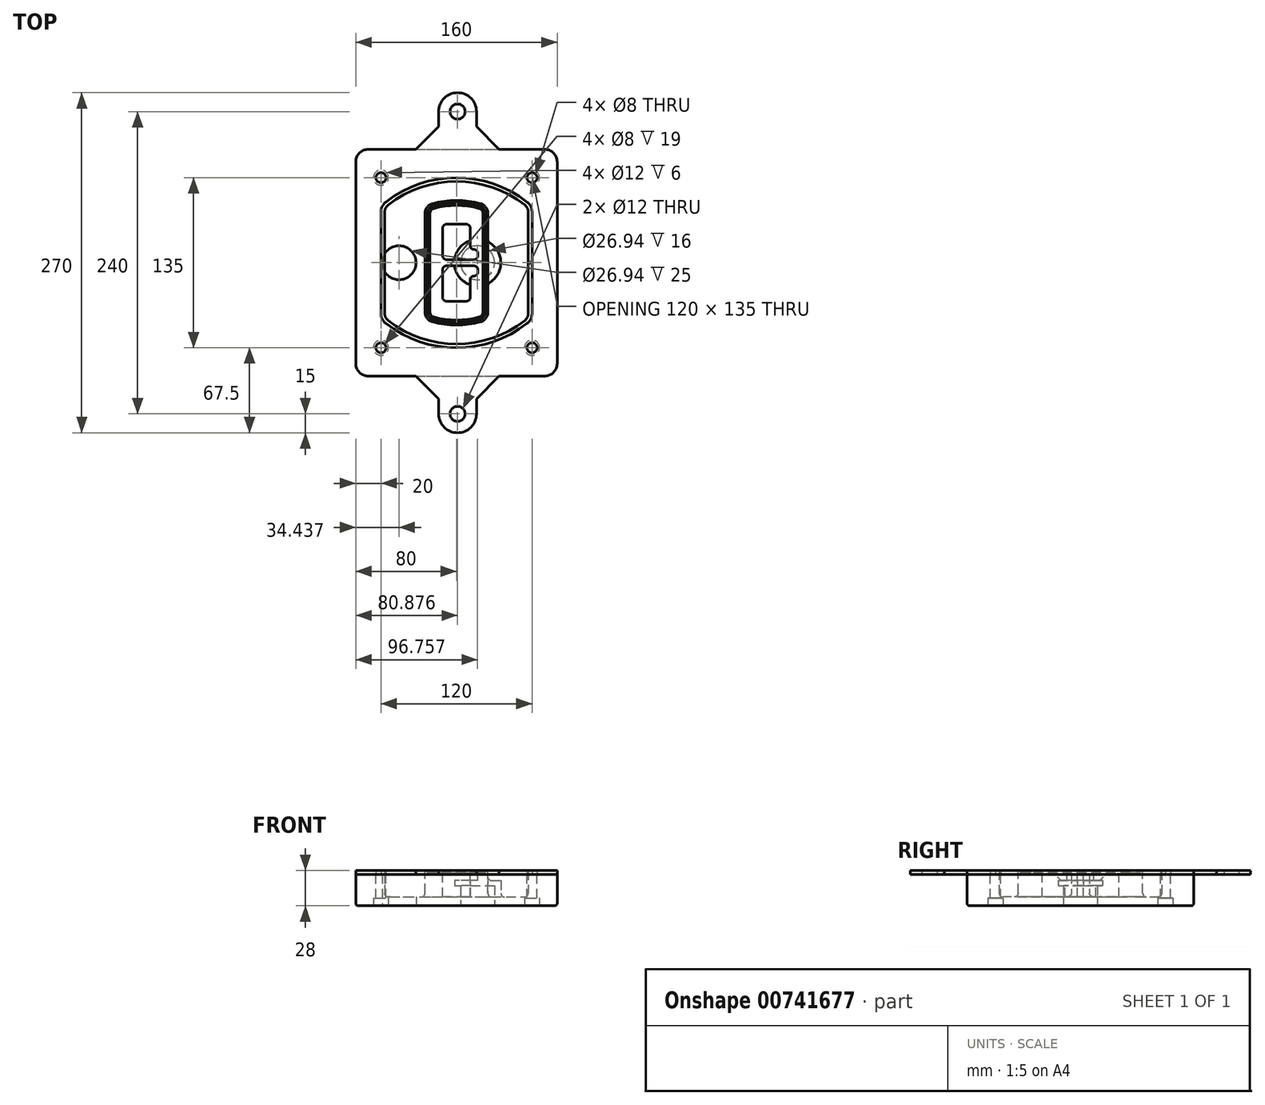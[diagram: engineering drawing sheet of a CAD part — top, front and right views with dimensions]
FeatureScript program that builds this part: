
annotation { "Feature Type Name" : "Feature", "Feature Type Description" : "" }
export const myFeature = defineFeature(function(context is Context, id is Id, definition is map)
    precondition{}
    {
        {
            var Q0;
            Q0=qCreatedBy(makeId("Top.planeOp"),FACE);
            var sketch = newSketch(context, id + "F0", { "sketchPlane" : qUnion([Q0])});
            skPoint(sketch, "E0.rect.middle", {"position": v(0, 0) * mm});
            skLineSegment(sketch, "E1.bottom", {"start": v(-70, -90) * mm, "end": v(70, -90) * mm});
            skLineSegment(sketch, "E1.top", {"start": v(-70, 90) * mm, "end": v(70, 90) * mm});
            skLineSegment(sketch, "E1.left", {"start": v(-80, -80) * mm, "end": v(-80, 80) * mm});
            skLineSegment(sketch, "E1.right", {"start": v(80, -80) * mm, "end": v(80, 80) * mm});
            skLineSegment(sketch, "E2", {"start": v(-80, 90) * mm, "end": v(80, -90) * mm, "construction": true});
            skLineSegment(sketch, "E3", {"start": v(80, 90) * mm, "end": v(-80, -90) * mm, "construction": true});
            skCircle(sketch, "E4", {"center": v(-60, 67.5) * mm, "radius": 4 * mm});
            skCircle(sketch, "E5", {"center": v(60, 67.5) * mm, "radius": 4 * mm});
            skCircle(sketch, "E6", {"center": v(60, -67.5) * mm, "radius": 4 * mm});
            skCircle(sketch, "E7", {"center": v(-60, -67.5) * mm, "radius": 4 * mm});
            skLineSegment(sketch, "E8", {"start": v(-60, 67.5) * mm, "end": v(60, 67.5) * mm, "construction": true});
            skLineSegment(sketch, "E9", {"start": v(60, 67.5) * mm, "end": v(60, -67.5) * mm, "construction": true});
            skLineSegment(sketch, "E10", {"start": v(60, -67.5) * mm, "end": v(-60, -67.5) * mm, "construction": true});
            skLineSegment(sketch, "E11", {"start": v(-60, -67.5) * mm, "end": v(-60, 67.5) * mm, "construction": true});
            skLineSegment(sketch, "E12", {"start": v(-60, 40.3) * mm, "end": v(-60, -40.3) * mm});
            skLineSegment(sketch, "E13", {"start": v(60, 40.3) * mm, "end": v(60, -40.3) * mm});
            skArc(sketch, "E14", {"start": v(56.15, 48.18) * mm, "mid": v(0, 67.5) * mm, "end": v(-56.15, 48.18) * mm});
            skArc(sketch, "E15", {"start": v(-56.15, -48.18) * mm, "mid": v(0, -67.5) * mm, "end": v(56.15, -48.18) * mm});
            skLineSegment(sketch, "E16", {"start": v(-60, 0) * mm, "end": v(60, 0) * mm, "construction": true});
            skPoint(sketch, "E17.visualSharp", {"position": v(-60, -45) * mm});
            skArc(sketch, "E17.filletArc", {"start": v(-60, -40.3) * mm, "mid": v(-58.99, -44.68) * mm, "end": v(-56.15, -48.18) * mm});
            skPoint(sketch, "E18.visualSharp", {"position": v(-60, 45) * mm});
            skArc(sketch, "E18.filletArc", {"start": v(-56.15, 48.18) * mm, "mid": v(-58.99, 44.68) * mm, "end": v(-60, 40.3) * mm});
            skPoint(sketch, "E19.visualSharp", {"position": v(60, 45) * mm});
            skArc(sketch, "E19.filletArc", {"start": v(60, 40.3) * mm, "mid": v(58.99, 44.68) * mm, "end": v(56.15, 48.18) * mm});
            skPoint(sketch, "E20.visualSharp", {"position": v(60, -45) * mm});
            skArc(sketch, "E20.filletArc", {"start": v(56.15, -48.18) * mm, "mid": v(58.99, -44.68) * mm, "end": v(60, -40.3) * mm});
            skPoint(sketch, "E21.visualSharp", {"position": v(-80, 90) * mm});
            skArc(sketch, "E21.filletArc", {"start": v(-70, 90) * mm, "mid": v(-77.07, 87.07) * mm, "end": v(-80, 80) * mm});
            skPoint(sketch, "E22.visualSharp", {"position": v(80, 90) * mm});
            skArc(sketch, "E22.filletArc", {"start": v(80, 80) * mm, "mid": v(77.07, 87.07) * mm, "end": v(70, 90) * mm});
            skPoint(sketch, "E23.visualSharp", {"position": v(80, -90) * mm});
            skArc(sketch, "E23.filletArc", {"start": v(70, -90) * mm, "mid": v(77.07, -87.07) * mm, "end": v(80, -80) * mm});
            skPoint(sketch, "E24.visualSharp", {"position": v(-80, -90) * mm});
            skArc(sketch, "E24.filletArc", {"start": v(-80, -80) * mm, "mid": v(-77.07, -87.07) * mm, "end": v(-70, -90) * mm});
            skArc(sketch, "E25.0", {"start": v(57, 40.3) * mm, "mid": v(56.3, 43.36) * mm, "end": v(54.3, 45.81) * mm});
            skLineSegment(sketch, "E25.1", {"start": v(57, 40.3) * mm, "end": v(57, -40.3) * mm});
            skArc(sketch, "E25.2", {"start": v(54.3, -45.81) * mm, "mid": v(56.3, -43.36) * mm, "end": v(57, -40.3) * mm});
            skArc(sketch, "E25.3", {"start": v(-54.3, -45.81) * mm, "mid": v(0, -64.5) * mm, "end": v(54.3, -45.81) * mm});
            skArc(sketch, "E25.4", {"start": v(-57, -40.3) * mm, "mid": v(-56.3, -43.36) * mm, "end": v(-54.3, -45.81) * mm});
            skArc(sketch, "E25.5", {"start": v(54.3, 45.81) * mm, "mid": v(0, 64.5) * mm, "end": v(-54.3, 45.81) * mm});
            skLineSegment(sketch, "E25.6", {"start": v(-57, 40.3) * mm, "end": v(-57, -40.3) * mm});
            skArc(sketch, "E25.7", {"start": v(-54.3, 45.81) * mm, "mid": v(-56.3, 43.36) * mm, "end": v(-57, 40.3) * mm});
            skArc(sketch, "E26.0", {"start": v(-58.62, 51.33) * mm, "mid": v(-62.58, 46.43) * mm, "end": v(-64, 40.3) * mm});
            skArc(sketch, "E26.1", {"start": v(58.62, 51.33) * mm, "mid": v(0, 71.5) * mm, "end": v(-58.62, 51.33) * mm});
            skArc(sketch, "E26.2", {"start": v(64, 40.3) * mm, "mid": v(62.58, 46.43) * mm, "end": v(58.62, 51.33) * mm});
            skLineSegment(sketch, "E26.3", {"start": v(64, 40.3) * mm, "end": v(64, -40.3) * mm});
            skArc(sketch, "E26.4", {"start": v(58.62, -51.33) * mm, "mid": v(62.58, -46.43) * mm, "end": v(64, -40.3) * mm});
            skLineSegment(sketch, "E26.5", {"start": v(-64, 40.3) * mm, "end": v(-64, -40.3) * mm});
            skArc(sketch, "E26.6", {"start": v(-58.62, -51.33) * mm, "mid": v(0, -71.5) * mm, "end": v(58.62, -51.33) * mm});
            skArc(sketch, "E26.7", {"start": v(-64, -40.3) * mm, "mid": v(-62.58, -46.43) * mm, "end": v(-58.62, -51.33) * mm});
            skSolve(sketch);
        }
        {
            var Q0;
            Q0=makeQuery(id+"F0.imprint","IMPRINT",FACE,{"disambiguationData":[TD([[makeQuery(id+"F0.imprint","IMPRINT",EDGE,{"derivedFrom":sQuery(id+"F0.wireOp",EDGE,"E1.bottom")}),1.0]])]});
            var Q1;
            Q1=makeQuery(id+"F0.imprint","IMPRINT",FACE,{"disambiguationData":[TD([[makeQuery(id+"F0.imprint","IMPRINT",EDGE,{"derivedFrom":sQuery(id+"F0.wireOp",EDGE,"E12")}),1.0]])]});
            var Q2;
            Q2=makeQuery(id+"F0.imprint","IMPRINT",FACE,{"disambiguationData":[TD([[makeQuery(id+"F0.imprint","IMPRINT",EDGE,{"derivedFrom":sQuery(id+"F0.wireOp",EDGE,"E25.0")}),1.0]])]});
            var Q3;
            Q3=makeQuery(id+"F0.imprint","IMPRINT",FACE,{"disambiguationData":[TD([[makeQuery(id+"F0.imprint","IMPRINT",EDGE,{"derivedFrom":sQuery(id+"F0.wireOp",EDGE,"E12")}),-1.0]])]});
            extrude(context, id + "F1", {"entities" : qUnion([Q0, Q1, Q2, Q3]), "oppositeDirection" : true, "depth" : 25 * mm});
        }
        {
            var Q0;
            Q0=makeQuery(id+"F0.imprint","IMPRINT",FACE,{"disambiguationData":[TD([[makeQuery(id+"F0.imprint","IMPRINT",EDGE,{"derivedFrom":sQuery(id+"F0.wireOp",EDGE,"E12")}),1.0]])]});
            extrude(context, id + "F2", {"entities" : qUnion([Q0]), "operationType" : NewBodyOperationType.ADD, "depth" : 3 * mm});
        }
        {
            var Q0;
            Q0=makeQuery(id+"F0.imprint","IMPRINT",FACE,{"disambiguationData":[TD([[makeQuery(id+"F0.imprint","IMPRINT",EDGE,{"derivedFrom":sQuery(id+"F0.wireOp",EDGE,"E25.0")}),1.0]])]});
            extrude(context, id + "F3", {"entities" : qUnion([Q0]), "operationType" : NewBodyOperationType.REMOVE, "oppositeDirection" : true, "depth" : 18 * mm});
        }
        {
            var Q0;
            Q0=makeQuery(id+"F2.opExtrude","CAP_FACE",FACE,{"disambiguationData":[OSD([sQuery(id+"F0.wireOp",EDGE,"E12"),sQuery(id+"F0.wireOp",EDGE,"E13"),sQuery(id+"F0.wireOp",EDGE,"E14"),sQuery(id+"F0.wireOp",EDGE,"E15"),sQuery(id+"F0.wireOp",EDGE,"E17.filletArc"),sQuery(id+"F0.wireOp",EDGE,"E18.filletArc"),sQuery(id+"F0.wireOp",EDGE,"E19.filletArc"),sQuery(id+"F0.wireOp",EDGE,"E20.filletArc"),sQuery(id+"F0.wireOp",EDGE,"E25.0"),sQuery(id+"F0.wireOp",EDGE,"E25.1"),sQuery(id+"F0.wireOp",EDGE,"E25.2"),sQuery(id+"F0.wireOp",EDGE,"E25.3"),sQuery(id+"F0.wireOp",EDGE,"E25.4"),sQuery(id+"F0.wireOp",EDGE,"E25.5"),sQuery(id+"F0.wireOp",EDGE,"E25.6"),sQuery(id+"F0.wireOp",EDGE,"E25.7")])],"isStart":false});
            var sketch = newSketch(context, id + "F4", { "sketchPlane" : qUnion([Q0])});
            skArc(sketch, "E27.0", {"start": v(-19.08, -46.97) * mm, "mid": v(0, -49.5) * mm, "end": v(19.08, -46.97) * mm});
            skArc(sketch, "E28.0", {"start": v(19.08, 46.97) * mm, "mid": v(0, 49.5) * mm, "end": v(-19.08, 46.97) * mm});
            skLineSegment(sketch, "E29", {"start": v(-25, 39.25) * mm, "end": v(-25, -39.25) * mm});
            skLineSegment(sketch, "E30", {"start": v(25, 39.25) * mm, "end": v(25, -39.25) * mm});
            skLineSegment(sketch, "E31", {"start": v(-25, 45.1) * mm, "end": v(25, 45.1) * mm, "construction": true});
            skLineSegment(sketch, "E32", {"start": v(-25, -45.1) * mm, "end": v(25, -45.1) * mm, "construction": true});
            skPoint(sketch, "E33.visualSharp", {"position": v(-25, 45.1) * mm});
            skArc(sketch, "E33.filletArc", {"start": v(-19.08, 46.97) * mm, "mid": v(-23.35, 44.11) * mm, "end": v(-25, 39.25) * mm});
            skPoint(sketch, "E34.visualSharp", {"position": v(25, 45.1) * mm});
            skArc(sketch, "E34.filletArc", {"start": v(25, 39.25) * mm, "mid": v(23.35, 44.11) * mm, "end": v(19.08, 46.97) * mm});
            skPoint(sketch, "E35.visualSharp", {"position": v(25, -45.1) * mm});
            skArc(sketch, "E35.filletArc", {"start": v(19.08, -46.97) * mm, "mid": v(23.35, -44.11) * mm, "end": v(25, -39.25) * mm});
            skPoint(sketch, "E36.visualSharp", {"position": v(-25, -45.1) * mm});
            skArc(sketch, "E36.filletArc", {"start": v(-25, -39.25) * mm, "mid": v(-23.35, -44.11) * mm, "end": v(-19.08, -46.97) * mm});
            skArc(sketch, "E37.0", {"start": v(54.3, 45.81) * mm, "mid": v(0, 64.5) * mm, "end": v(-54.3, 45.81) * mm});
            skArc(sketch, "E37.1", {"start": v(-54.3, 45.81) * mm, "mid": v(-56.3, 43.36) * mm, "end": v(-57, 40.3) * mm});
            skLineSegment(sketch, "E37.2", {"start": v(-57, 40.3) * mm, "end": v(-57, -40.3) * mm});
            skArc(sketch, "E37.3", {"start": v(-57, -40.3) * mm, "mid": v(-56.3, -43.36) * mm, "end": v(-54.3, -45.81) * mm});
            skArc(sketch, "E37.4", {"start": v(-54.3, -45.81) * mm, "mid": v(0, -64.5) * mm, "end": v(54.3, -45.81) * mm});
            skArc(sketch, "E37.5", {"start": v(54.3, -45.81) * mm, "mid": v(56.3, -43.36) * mm, "end": v(57, -40.3) * mm});
            skLineSegment(sketch, "E37.6", {"start": v(57, 40.3) * mm, "end": v(57, -40.3) * mm});
            skArc(sketch, "E37.7", {"start": v(57, 40.3) * mm, "mid": v(56.3, 43.36) * mm, "end": v(54.3, 45.81) * mm});
            skLineSegment(sketch, "E38.0", {"start": v(23, 39.25) * mm, "end": v(23, -39.25) * mm});
            skArc(sketch, "E38.1", {"start": v(18.56, -45.04) * mm, "mid": v(21.76, -42.9) * mm, "end": v(23, -39.25) * mm});
            skArc(sketch, "E38.2", {"start": v(-18.56, -45.04) * mm, "mid": v(0, -47.5) * mm, "end": v(18.56, -45.04) * mm});
            skArc(sketch, "E38.3", {"start": v(-23, -39.25) * mm, "mid": v(-21.76, -42.9) * mm, "end": v(-18.56, -45.04) * mm});
            skLineSegment(sketch, "E38.4", {"start": v(-23, 39.25) * mm, "end": v(-23, -39.25) * mm});
            skArc(sketch, "E38.5", {"start": v(23, 39.25) * mm, "mid": v(21.76, 42.9) * mm, "end": v(18.56, 45.04) * mm});
            skArc(sketch, "E38.6", {"start": v(-18.56, 45.04) * mm, "mid": v(-21.76, 42.9) * mm, "end": v(-23, 39.25) * mm});
            skArc(sketch, "E38.7", {"start": v(18.56, 45.04) * mm, "mid": v(0, 47.5) * mm, "end": v(-18.56, 45.04) * mm});
            skArc(sketch, "E39.0", {"start": v(21, 39.25) * mm, "mid": v(20.18, 41.68) * mm, "end": v(18.04, 43.1) * mm});
            skLineSegment(sketch, "E39.1", {"start": v(21, 39.25) * mm, "end": v(21, -39.25) * mm});
            skArc(sketch, "E39.2", {"start": v(18.04, -43.1) * mm, "mid": v(20.18, -41.68) * mm, "end": v(21, -39.25) * mm});
            skArc(sketch, "E39.3", {"start": v(-18.04, -43.1) * mm, "mid": v(0, -45.5) * mm, "end": v(18.04, -43.1) * mm});
            skArc(sketch, "E39.4", {"start": v(-21, -39.25) * mm, "mid": v(-20.18, -41.68) * mm, "end": v(-18.04, -43.1) * mm});
            skArc(sketch, "E39.5", {"start": v(18.04, 43.1) * mm, "mid": v(0, 45.5) * mm, "end": v(-18.04, 43.1) * mm});
            skLineSegment(sketch, "E39.6", {"start": v(-21, 39.25) * mm, "end": v(-21, -39.25) * mm});
            skArc(sketch, "E39.7", {"start": v(-18.04, 43.1) * mm, "mid": v(-20.18, 41.68) * mm, "end": v(-21, 39.25) * mm});
            skLineSegment(sketch, "E40", {"start": v(-25, 0) * mm, "end": v(25, 0) * mm, "construction": true});
            skLineSegment(sketch, "E41", {"start": v(-11, 5.5) * mm, "end": v(-11, 27.5) * mm});
            skLineSegment(sketch, "E42", {"start": v(-8, 30.5) * mm, "end": v(8, 30.5) * mm});
            skLineSegment(sketch, "E43", {"start": v(11, 27.5) * mm, "end": v(11, 13.5) * mm});
            skLineSegment(sketch, "E44", {"start": v(14, 10.5) * mm, "end": v(14, 10.5) * mm});
            skLineSegment(sketch, "E45", {"start": v(17, 7.5) * mm, "end": v(17, 5.5) * mm});
            skLineSegment(sketch, "E46", {"start": v(14, 2.5) * mm, "end": v(-8, 2.5) * mm});
            skPoint(sketch, "E47.visualSharp", {"position": v(-11, 30.5) * mm});
            skArc(sketch, "E47.filletArc", {"start": v(-8, 30.5) * mm, "mid": v(-10.12, 29.62) * mm, "end": v(-11, 27.5) * mm});
            skPoint(sketch, "E48.visualSharp", {"position": v(11, 30.5) * mm});
            skArc(sketch, "E48.filletArc", {"start": v(11, 27.5) * mm, "mid": v(10.12, 29.62) * mm, "end": v(8, 30.5) * mm});
            skPoint(sketch, "E49.visualSharp", {"position": v(11, 10.5) * mm});
            skArc(sketch, "E49.filletArc", {"start": v(11, 13.5) * mm, "mid": v(11.88, 11.38) * mm, "end": v(14, 10.5) * mm});
            skPoint(sketch, "E50.visualSharp", {"position": v(17, 10.5) * mm});
            skArc(sketch, "E50.filletArc", {"start": v(17, 7.5) * mm, "mid": v(16.12, 9.62) * mm, "end": v(14, 10.5) * mm});
            skPoint(sketch, "E51.visualSharp", {"position": v(17, 2.5) * mm});
            skArc(sketch, "E51.filletArc", {"start": v(14, 2.5) * mm, "mid": v(16.12, 3.38) * mm, "end": v(17, 5.5) * mm});
            skPoint(sketch, "E52.visualSharp", {"position": v(-11, 2.5) * mm});
            skArc(sketch, "E52.filletArc", {"start": v(-11, 5.5) * mm, "mid": v(-10.12, 3.38) * mm, "end": v(-8, 2.5) * mm});
            skLineSegment(sketch, "E53.0.MirrorCS", {"start": v(14, -2.5) * mm, "end": v(-8, -2.5) * mm});
            skArc(sketch, "E54.0.MirrorCS", {"start": v(-11, -5.5) * mm, "mid": v(-10.12, -3.38) * mm, "end": v(-8, -2.5) * mm});
            skLineSegment(sketch, "E55.0.MirrorCS", {"start": v(-11, -5.5) * mm, "end": v(-11, -27.5) * mm});
            skArc(sketch, "E56.0.MirrorCS", {"start": v(-8, -30.5) * mm, "mid": v(-10.12, -29.62) * mm, "end": v(-11, -27.5) * mm});
            skLineSegment(sketch, "E57.0.MirrorCS", {"start": v(-8, -30.5) * mm, "end": v(8, -30.5) * mm});
            skArc(sketch, "E58.0.MirrorCS", {"start": v(11, -27.5) * mm, "mid": v(10.12, -29.62) * mm, "end": v(8, -30.5) * mm});
            skLineSegment(sketch, "E59.0.MirrorCS", {"start": v(11, -27.5) * mm, "end": v(11, -13.5) * mm});
            skArc(sketch, "E60.0.MirrorCS", {"start": v(11, -13.5) * mm, "mid": v(11.88, -11.38) * mm, "end": v(14, -10.5) * mm});
            skArc(sketch, "E61.0.MirrorCS", {"start": v(17, -7.5) * mm, "mid": v(16.12, -9.62) * mm, "end": v(14, -10.5) * mm});
            skLineSegment(sketch, "E62.0.MirrorCS", {"start": v(17, -7.5) * mm, "end": v(17, -5.5) * mm});
            skArc(sketch, "E63.0.MirrorCS", {"start": v(14, -2.5) * mm, "mid": v(16.12, -3.38) * mm, "end": v(17, -5.5) * mm});
            skSolve(sketch);
        }
        {
            var Q0;
            Q0=makeQuery(id+"F4.imprint","IMPRINT",FACE,{"disambiguationData":[TD([[makeQuery(id+"F4.imprint","IMPRINT",EDGE,{"derivedFrom":sQuery(id+"F4.wireOp",EDGE,"E27.0")}),1.0]])]});
            var Q1;
            Q1=makeQuery(id+"F4.imprint","IMPRINT",FACE,{"disambiguationData":[TD([[makeQuery(id+"F4.imprint","IMPRINT",EDGE,{"derivedFrom":sQuery(id+"F4.wireOp",EDGE,"E38.0")}),-1.0]])]});
            var Q2;
            Q2=makeQuery(id+"F4.imprint","IMPRINT",FACE,{"disambiguationData":[TD([[makeQuery(id+"F4.imprint","IMPRINT",EDGE,{"derivedFrom":sQuery(id+"F4.wireOp",EDGE,"E39.0")}),1.0]])]});
            extrude(context, id + "F5", {"entities" : qUnion([Q0, Q1, Q2]), "operationType" : NewBodyOperationType.ADD, "endBound" : BoundingType.UP_TO_NEXT, "oppositeDirection" : true, "depth" : 25 * mm});
        }
        {
            var Q0;
            Q0=makeQuery(id+"F4.imprint","IMPRINT",FACE,{"disambiguationData":[TD([[makeQuery(id+"F4.imprint","IMPRINT",EDGE,{"derivedFrom":sQuery(id+"F4.wireOp",EDGE,"E38.0")}),-1.0]])]});
            extrude(context, id + "F6", {"entities" : qUnion([Q0]), "operationType" : NewBodyOperationType.REMOVE, "oppositeDirection" : true, "depth" : 2 * mm});
        }
        {
            var Q0;
            Q0=makeQuery(id+"F1.opExtrude","CAP_FACE",FACE,{"disambiguationData":[OSD([sQuery(id+"F0.wireOp",EDGE,"E1.bottom"),sQuery(id+"F0.wireOp",EDGE,"E1.top"),sQuery(id+"F0.wireOp",EDGE,"E1.left"),sQuery(id+"F0.wireOp",EDGE,"E1.right"),sQuery(id+"F0.wireOp",EDGE,"E4"),sQuery(id+"F0.wireOp",EDGE,"E5"),sQuery(id+"F0.wireOp",EDGE,"E6"),sQuery(id+"F0.wireOp",EDGE,"E7"),sQuery(id+"F0.wireOp",EDGE,"E21.filletArc"),sQuery(id+"F0.wireOp",EDGE,"E22.filletArc"),sQuery(id+"F0.wireOp",EDGE,"E23.filletArc"),sQuery(id+"F0.wireOp",EDGE,"E24.filletArc")])],"isStart":false});
            var sketch = newSketch(context, id + "F7", { "sketchPlane" : qUnion([Q0])});
            skCircle(sketch, "E64", {"center": v(16.76, 0) * mm, "radius": 13.47 * mm});
            skCircle(sketch, "E65", {"center": v(-45.56, 0) * mm, "radius": 13.47 * mm});
            skLineSegment(sketch, "E66", {"start": v(80, 0) * mm, "end": v(-80, 0) * mm});
            skCircle(sketch, "E67", {"center": v(16.76, 0) * mm, "radius": 18.47 * mm});
            skCircle(sketch, "E68", {"center": v(60, -67.5) * mm, "radius": 6 * mm});
            skCircle(sketch, "E69", {"center": v(-60, -67.5) * mm, "radius": 6 * mm});
            skCircle(sketch, "E70", {"center": v(-60, 67.5) * mm, "radius": 6 * mm});
            skCircle(sketch, "E71", {"center": v(60, 67.5) * mm, "radius": 6 * mm});
            skSolve(sketch);
        }
        {
            var Q0;
            {var subQ1=sQuery(id+"F7.wireOp",EDGE,"E66");var subQ4=sQuery(id+"F7.wireOp",EDGE,"E64");var subQ6=makeQuery(id+"F7.imprint","INTERSECT",VERTEX,{"disambiguationData":[OD(0.0)],"derivedFrom":[subQ4,subQ1]});Q0=makeQuery(id+"F7.imprint","IMPRINT",FACE,{"disambiguationData":[TD([[makeQuery(id+"F7.imprint","IMPRINT",EDGE,{"disambiguationData":[TD([[subQ6,-1.0]])],"derivedFrom":subQ4}),-1.0]])]});}
            var Q1;
            {var subQ0=sQuery(id+"F7.wireOp",EDGE,"E66");var subQ1=sQuery(id+"F7.wireOp",EDGE,"E64");var subQ3=makeQuery(id+"F7.imprint","INTERSECT",VERTEX,{"disambiguationData":[OD(0.0)],"derivedFrom":[subQ1,subQ0]});Q1=makeQuery(id+"F7.imprint","IMPRINT",FACE,{"disambiguationData":[TD([[makeQuery(id+"F7.imprint","IMPRINT",EDGE,{"disambiguationData":[TD([[subQ3,-1.0]])],"derivedFrom":subQ1}),1.0]])]});}
            var Q2;
            {var subQ0=sQuery(id+"F7.wireOp",EDGE,"E66");var subQ1=sQuery(id+"F7.wireOp",EDGE,"E64");var subQ3=makeQuery(id+"F7.imprint","INTERSECT",VERTEX,{"disambiguationData":[OD(0.0)],"derivedFrom":[subQ1,subQ0]});Q2=makeQuery(id+"F7.imprint","IMPRINT",FACE,{"disambiguationData":[TD([[makeQuery(id+"F7.imprint","IMPRINT",EDGE,{"disambiguationData":[TD([[subQ3,1.0]])],"derivedFrom":subQ1}),1.0]])]});}
            var Q3;
            {var subQ1=sQuery(id+"F7.wireOp",EDGE,"E66");var subQ4=sQuery(id+"F7.wireOp",EDGE,"E64");var subQ6=makeQuery(id+"F7.imprint","INTERSECT",VERTEX,{"disambiguationData":[OD(0.0)],"derivedFrom":[subQ4,subQ1]});Q3=makeQuery(id+"F7.imprint","IMPRINT",FACE,{"disambiguationData":[TD([[makeQuery(id+"F7.imprint","IMPRINT",EDGE,{"disambiguationData":[TD([[subQ6,1.0]])],"derivedFrom":subQ4}),-1.0]])]});}
            extrude(context, id + "F8", {"entities" : qUnion([Q0, Q1, Q2, Q3]), "operationType" : NewBodyOperationType.ADD, "oppositeDirection" : true, "depth" : 20 * mm});
        }
        {
            var Q0;
            {var subQ0=sQuery(id+"F7.wireOp",EDGE,"E66");var subQ1=sQuery(id+"F7.wireOp",EDGE,"E64");var subQ3=makeQuery(id+"F7.imprint","INTERSECT",VERTEX,{"disambiguationData":[OD(0.0)],"derivedFrom":[subQ1,subQ0]});Q0=makeQuery(id+"F7.imprint","IMPRINT",FACE,{"disambiguationData":[TD([[makeQuery(id+"F7.imprint","IMPRINT",EDGE,{"disambiguationData":[TD([[subQ3,-1.0]])],"derivedFrom":subQ1}),1.0]])]});}
            var Q1;
            {var subQ0=sQuery(id+"F7.wireOp",EDGE,"E66");var subQ1=sQuery(id+"F7.wireOp",EDGE,"E64");var subQ3=makeQuery(id+"F7.imprint","INTERSECT",VERTEX,{"disambiguationData":[OD(0.0)],"derivedFrom":[subQ1,subQ0]});Q1=makeQuery(id+"F7.imprint","IMPRINT",FACE,{"disambiguationData":[TD([[makeQuery(id+"F7.imprint","IMPRINT",EDGE,{"disambiguationData":[TD([[subQ3,1.0]])],"derivedFrom":subQ1}),1.0]])]});}
            extrude(context, id + "F9", {"entities" : qUnion([Q0, Q1]), "operationType" : NewBodyOperationType.REMOVE, "oppositeDirection" : true, "depth" : 16 * mm});
        }
        {
            var Q0;
            {var subQ0=sQuery(id+"F7.wireOp",EDGE,"E66");var subQ1=sQuery(id+"F7.wireOp",EDGE,"E65");var subQ3=makeQuery(id+"F7.imprint","INTERSECT",VERTEX,{"disambiguationData":[OD(0.0)],"derivedFrom":[subQ1,subQ0]});Q0=makeQuery(id+"F7.imprint","IMPRINT",FACE,{"disambiguationData":[TD([[makeQuery(id+"F7.imprint","IMPRINT",EDGE,{"disambiguationData":[TD([[subQ3,-1.0]])],"derivedFrom":subQ1}),1.0]])]});}
            var Q1;
            {var subQ0=sQuery(id+"F7.wireOp",EDGE,"E66");var subQ1=sQuery(id+"F7.wireOp",EDGE,"E65");var subQ3=makeQuery(id+"F7.imprint","INTERSECT",VERTEX,{"disambiguationData":[OD(0.0)],"derivedFrom":[subQ1,subQ0]});Q1=makeQuery(id+"F7.imprint","IMPRINT",FACE,{"disambiguationData":[TD([[makeQuery(id+"F7.imprint","IMPRINT",EDGE,{"disambiguationData":[TD([[subQ3,1.0]])],"derivedFrom":subQ1}),1.0]])]});}
            extrude(context, id + "F10", {"entities" : qUnion([Q0, Q1]), "operationType" : NewBodyOperationType.REMOVE, "oppositeDirection" : true, "depth" : 25 * mm});
        }
        {
            var Q0;
            Q0=makeQuery(id+"F7.imprint","IMPRINT",FACE,{"disambiguationData":[TD([[makeQuery(id+"F7.imprint","IMPRINT",EDGE,{"derivedFrom":sQuery(id+"F7.wireOp",EDGE,"E68")}),1.0]])]});
            var Q1;
            Q1=makeQuery(id+"F7.imprint","IMPRINT",FACE,{"disambiguationData":[TD([[makeQuery(id+"F7.imprint","IMPRINT",EDGE,{"derivedFrom":makeQuery(id+"F1.opExtrude","CAP_EDGE",EDGE,{"disambiguationData":[OSD([sQuery(id+"F0.wireOp",EDGE,"E5")])],"isStart":false})}),-1.0]])]});
            var Q2;
            Q2=makeQuery(id+"F7.imprint","IMPRINT",FACE,{"disambiguationData":[TD([[makeQuery(id+"F7.imprint","IMPRINT",EDGE,{"derivedFrom":sQuery(id+"F7.wireOp",EDGE,"E69")}),1.0]])]});
            var Q3;
            Q3=makeQuery(id+"F7.imprint","IMPRINT",FACE,{"disambiguationData":[TD([[makeQuery(id+"F7.imprint","IMPRINT",EDGE,{"derivedFrom":makeQuery(id+"F1.opExtrude","CAP_EDGE",EDGE,{"disambiguationData":[OSD([sQuery(id+"F0.wireOp",EDGE,"E4")])],"isStart":false})}),-1.0]])]});
            var Q4;
            Q4=makeQuery(id+"F7.imprint","IMPRINT",FACE,{"disambiguationData":[TD([[makeQuery(id+"F7.imprint","IMPRINT",EDGE,{"derivedFrom":sQuery(id+"F7.wireOp",EDGE,"E70")}),1.0]])]});
            var Q5;
            Q5=makeQuery(id+"F7.imprint","IMPRINT",FACE,{"disambiguationData":[TD([[makeQuery(id+"F7.imprint","IMPRINT",EDGE,{"derivedFrom":makeQuery(id+"F1.opExtrude","CAP_EDGE",EDGE,{"disambiguationData":[OSD([sQuery(id+"F0.wireOp",EDGE,"E7")])],"isStart":false})}),-1.0]])]});
            var Q6;
            Q6=makeQuery(id+"F7.imprint","IMPRINT",FACE,{"disambiguationData":[TD([[makeQuery(id+"F7.imprint","IMPRINT",EDGE,{"derivedFrom":sQuery(id+"F7.wireOp",EDGE,"E71")}),1.0]])]});
            var Q7;
            Q7=makeQuery(id+"F7.imprint","IMPRINT",FACE,{"disambiguationData":[TD([[makeQuery(id+"F7.imprint","IMPRINT",EDGE,{"derivedFrom":makeQuery(id+"F1.opExtrude","CAP_EDGE",EDGE,{"disambiguationData":[OSD([sQuery(id+"F0.wireOp",EDGE,"E6")])],"isStart":false})}),-1.0]])]});
            extrude(context, id + "F11", {"entities" : qUnion([Q0, Q1, Q2, Q3, Q4, Q5, Q6, Q7]), "operationType" : NewBodyOperationType.REMOVE, "oppositeDirection" : true, "depth" : 6 * mm});
        }
        {
            var Q0;
            Q0=makeQuery(id+"F9.boolean.opBoolean","COPY",FACE,{"derivedFrom":makeQuery(id+"F9.opExtrude","CAP_FACE",FACE,{"disambiguationData":[OSD([sQuery(id+"F7.wireOp",EDGE,"E64")])],"isStart":false})});
            var sketch = newSketch(context, id + "F12", { "sketchPlane" : qUnion([Q0])});
            skArc(sketch, "E72.0", {"start": v(11, 17.55) * mm, "mid": v(2.57, 11.82) * mm, "end": v(-1.54, 2.5) * mm});
            skArc(sketch, "E72.1", {"start": v(-1.54, -2.5) * mm, "mid": v(2.57, -11.82) * mm, "end": v(11, -17.55) * mm});
            skLineSegment(sketch, "E73", {"start": v(-1.54, -2.5) * mm, "end": v(14, -2.5) * mm});
            skLineSegment(sketch, "E74.0", {"start": v(14, 2.5) * mm, "end": v(-1.54, 2.5) * mm});
            skArc(sketch, "E74.1", {"start": v(14, 2.5) * mm, "mid": v(16.12, 3.38) * mm, "end": v(17, 5.5) * mm});
            skLineSegment(sketch, "E74.2", {"start": v(17, 7.5) * mm, "end": v(17, 5.5) * mm});
            skArc(sketch, "E74.3", {"start": v(17, 7.5) * mm, "mid": v(16.12, 9.62) * mm, "end": v(14, 10.5) * mm});
            skArc(sketch, "E74.4", {"start": v(11, 13.5) * mm, "mid": v(11.88, 11.38) * mm, "end": v(14, 10.5) * mm});
            skLineSegment(sketch, "E74.5", {"start": v(11, 17.55) * mm, "end": v(11, 13.5) * mm});
            skLineSegment(sketch, "E74.7", {"start": v(14, -2.5) * mm, "end": v(-1.54, -2.5) * mm});
            skArc(sketch, "E74.8", {"start": v(14, -2.5) * mm, "mid": v(16.12, -3.38) * mm, "end": v(17, -5.5) * mm});
            skLineSegment(sketch, "E74.9", {"start": v(17, -7.5) * mm, "end": v(17, -5.5) * mm});
            skArc(sketch, "E74.10", {"start": v(17, -7.5) * mm, "mid": v(16.12, -9.62) * mm, "end": v(14, -10.5) * mm});
            skArc(sketch, "E74.11", {"start": v(11, -13.5) * mm, "mid": v(11.88, -11.38) * mm, "end": v(14, -10.5) * mm});
            skLineSegment(sketch, "E74.12", {"start": v(11, -17.55) * mm, "end": v(11, -13.5) * mm});
            skPoint(sketch, "E75.orphan", {"position": v(11, -27.5) * mm});
            skPoint(sketch, "E76.orphan", {"position": v(-8, -2.5) * mm});
            skPoint(sketch, "E77.orphan", {"position": v(-8, 2.5) * mm});
            skPoint(sketch, "E78.orphan", {"position": v(11, 27.5) * mm});
            skSolve(sketch);
        }
        {
            var Q0;
            {var subQ7=sQuery(id+"F12.wireOp",EDGE,"E72.0");var subQ14=sQuery(id+"F12.wireOp",EDGE,"E72.1");var subQ16=sQuery(id+"F12.wireOp",EDGE,"E74.1");var subQ18=sQuery(id+"F12.wireOp",EDGE,"E74.8");Q0=qUnion([makeQuery(id+"F12.imprint","IMPRINT",FACE,{"disambiguationData":[TD([[makeQuery(id+"F12.imprint","IMPRINT",EDGE,{"derivedFrom":subQ7}),1.0]])]}),makeQuery(id+"F12.imprint","IMPRINT",FACE,{"disambiguationData":[TD([[makeQuery(id+"F12.imprint","IMPRINT",EDGE,{"derivedFrom":subQ14}),1.0]])]}),makeQuery(id+"F12.imprint","IMPRINT",FACE,{"disambiguationData":[TD([[makeQuery(id+"F12.imprint","IMPRINT",EDGE,{"derivedFrom":subQ16}),1.0]])]}),makeQuery(id+"F12.imprint","IMPRINT",FACE,{"disambiguationData":[TD([[makeQuery(id+"F12.imprint","IMPRINT",EDGE,{"derivedFrom":subQ18}),-1.0]])]})]);}
            var Q1;
            Q1=makeQuery(id+"F5.boolean.opBoolean","SPLIT",FACE,{"disambiguationData":[TD([makeQuery(id+"F5.opExtrude","SWEPT_FACE",FACE,{"disambiguationData":[OSD([sQuery(id+"F4.wireOp",EDGE,"E41")])]})])],"derivedFrom":makeQuery(id+"F3.boolean.opBoolean","COPY",FACE,{"derivedFrom":makeQuery(id+"F3.opExtrude","CAP_FACE",FACE,{"disambiguationData":[OSD([sQuery(id+"F0.wireOp",EDGE,"E25.0"),sQuery(id+"F0.wireOp",EDGE,"E25.1"),sQuery(id+"F0.wireOp",EDGE,"E25.2"),sQuery(id+"F0.wireOp",EDGE,"E25.3"),sQuery(id+"F0.wireOp",EDGE,"E25.4"),sQuery(id+"F0.wireOp",EDGE,"E25.5"),sQuery(id+"F0.wireOp",EDGE,"E25.6"),sQuery(id+"F0.wireOp",EDGE,"E25.7")])],"isStart":false})})});
            extrude(context, id + "F13", {"entities" : qUnion([Q0]), "operationType" : NewBodyOperationType.REMOVE, "endBound" : BoundingType.UP_TO_SURFACE, "endBoundEntityFace" : qUnion([Q1]), "depth" : 25 * mm});
        }
        {
            var Q0;
            Q0=makeQuery(id+"F3.boolean.opBoolean","COPY",EDGE,{"derivedFrom":makeQuery(id+"F3.opExtrude","CAP_EDGE",EDGE,{"disambiguationData":[OSD([sQuery(id+"F0.wireOp",EDGE,"E25.6")])],"isStart":false})});
            var Q1;
            Q1=makeQuery(id+"F8.boolean.opBoolean","INTERSECT",EDGE,{"derivedFrom":[makeQuery(id+"F5.opExtrude","SWEPT_FACE",FACE,{"disambiguationData":[OSD([sQuery(id+"F4.wireOp",EDGE,"E30")])]}),makeQuery(id+"F8.opExtrude","CAP_FACE",FACE,{"disambiguationData":[OSD([sQuery(id+"F7.wireOp",EDGE,"E67")])],"isStart":false})]});
            var Q2;
            Q2=makeQuery(id+"F8.boolean.opBoolean","INTERSECT",EDGE,{"disambiguationData":[OD(1.0)],"derivedFrom":[makeQuery(id+"F5.opExtrude","SWEPT_FACE",FACE,{"disambiguationData":[OSD([sQuery(id+"F4.wireOp",EDGE,"E30")])]}),makeQuery(id+"F8.opExtrude","SWEPT_FACE",FACE,{"disambiguationData":[OSD([sQuery(id+"F7.wireOp",EDGE,"E67")])]})]});
            var Q3;
            {var subQ0=sQuery(id+"F4.wireOp",EDGE,"E30");Q3=makeQuery(id+"F8.boolean.opBoolean","SPLIT",EDGE,{"disambiguationData":[TD([makeQuery(id+"F5.opExtrude","SWEPT_FACE",FACE,{"disambiguationData":[OSD([sQuery(id+"F4.wireOp",EDGE,"E35.filletArc")])]})])],"derivedFrom":makeQuery(id+"F5.opExtrude","CAP_EDGE",EDGE,{"disambiguationData":[OSD([subQ0])],"isStart":false})});}
            var Q4;
            {var subQ0=sQuery(id+"F0.wireOp",EDGE,"E25.7");var subQ1=sQuery(id+"F0.wireOp",EDGE,"E25.1");var subQ2=sQuery(id+"F0.wireOp",EDGE,"E25.6");var subQ3=sQuery(id+"F0.wireOp",EDGE,"E25.5");var subQ4=sQuery(id+"F0.wireOp",EDGE,"E25.4");var subQ5=sQuery(id+"F0.wireOp",EDGE,"E25.0");var subQ6=sQuery(id+"F0.wireOp",EDGE,"E25.2");var subQ7=sQuery(id+"F0.wireOp",EDGE,"E25.3");Q4=makeQuery(id+"F8.boolean.opBoolean","INTERSECT",EDGE,{"derivedFrom":[makeQuery(id+"F5.boolean.opBoolean","SPLIT",FACE,{"disambiguationData":[TD([makeQuery(id+"F2.opExtrude","SWEPT_FACE",FACE,{"disambiguationData":[OSD([subQ5])]})])],"derivedFrom":makeQuery(id+"F3.boolean.opBoolean","COPY",FACE,{"derivedFrom":makeQuery(id+"F3.opExtrude","CAP_FACE",FACE,{"disambiguationData":[OSD([subQ5,subQ1,subQ6,subQ7,subQ4,subQ3,subQ2,subQ0])],"isStart":false})})}),makeQuery(id+"F8.opExtrude","SWEPT_FACE",FACE,{"disambiguationData":[OSD([sQuery(id+"F7.wireOp",EDGE,"E67")])]})]});}
            var Q5;
            Q5=makeQuery(id+"F8.boolean.opBoolean","INTERSECT",EDGE,{"disambiguationData":[OD(0.0)],"derivedFrom":[makeQuery(id+"F5.opExtrude","SWEPT_FACE",FACE,{"disambiguationData":[OSD([sQuery(id+"F4.wireOp",EDGE,"E30")])]}),makeQuery(id+"F8.opExtrude","SWEPT_FACE",FACE,{"disambiguationData":[OSD([sQuery(id+"F7.wireOp",EDGE,"E67")])]})]});
            fillet(context, id + "F14", {"entities" : qUnion([Q0, Q1, Q2, Q3, Q4, Q5]), "radius" : 3 * mm, "tangentPropagation" : true, "allowEdgeOverflow" : false});
        }
        {
            var Q0;
            Q0=makeQuery(id+"F1.opExtrude","CAP_EDGE",EDGE,{"disambiguationData":[OSD([sQuery(id+"F0.wireOp",EDGE,"E1.bottom")])],"isStart":false});
            fillet(context, id + "F15", {"entities" : qUnion([Q0]), "radius" : 2 * mm, "tangentPropagation" : true, "allowEdgeOverflow" : false});
        }
        {
            var Q0;
            {var subQ0=sQuery(id+"F0.wireOp",EDGE,"E21.filletArc");var subQ1=sQuery(id+"F0.wireOp",EDGE,"E7");var subQ2=sQuery(id+"F0.wireOp",EDGE,"E6");var subQ3=sQuery(id+"F0.wireOp",EDGE,"E5");var subQ4=sQuery(id+"F0.wireOp",EDGE,"E4");var subQ5=sQuery(id+"F0.wireOp",EDGE,"E22.filletArc");var subQ6=sQuery(id+"F0.wireOp",EDGE,"E1.bottom");var subQ7=sQuery(id+"F0.wireOp",EDGE,"E1.right");var subQ8=sQuery(id+"F0.wireOp",EDGE,"E1.top");var subQ9=sQuery(id+"F0.wireOp",EDGE,"E1.left");var subQ10=sQuery(id+"F0.wireOp",EDGE,"E23.filletArc");var subQ11=sQuery(id+"F0.wireOp",EDGE,"E24.filletArc");Q0=makeQuery(id+"F2.boolean.opBoolean","SPLIT",FACE,{"disambiguationData":[TD([makeQuery(id+"F1.opExtrude","SWEPT_FACE",FACE,{"disambiguationData":[OSD([subQ6])]})])],"derivedFrom":makeQuery(id+"F1.opExtrude","CAP_FACE",FACE,{"disambiguationData":[OSD([subQ6,subQ8,subQ9,subQ7,subQ4,subQ3,subQ2,subQ1,subQ0,subQ5,subQ10,subQ11])],"isStart":true})});}
            var sketch = newSketch(context, id + "F16", { "sketchPlane" : qUnion([Q0])});
            skLineSegment(sketch, "E79", {"start": v(-32.12, 90) * mm, "end": v(-14.12, 108) * mm});
            skLineSegment(sketch, "E80", {"start": v(-14.12, 108) * mm, "end": v(-14.12, 120) * mm});
            skArc(sketch, "E81", {"start": v(15.88, 120) * mm, "mid": v(0.88, 135) * mm, "end": v(-14.12, 120) * mm});
            skPoint(sketch, "E82.orphan", {"position": v(0, 90) * mm});
            skPoint(sketch, "E83.startSnap0", {"position": v(0.88, 135) * mm});
            skPoint(sketch, "E83.end.orphan", {"position": v(0.88, 90) * mm});
            skPoint(sketch, "E83.start.orphan", {"position": v(0.88, 135) * mm});
            skLineSegment(sketch, "E84", {"start": v(0.88, 90) * mm, "end": v(0.88, 120) * mm, "construction": true});
            skCircle(sketch, "E85", {"center": v(0.88, 120) * mm, "radius": 6 * mm});
            skLineSegment(sketch, "E86", {"start": v(15.88, 120) * mm, "end": v(15.88, 108) * mm});
            skLineSegment(sketch, "E87", {"start": v(15.88, 108) * mm, "end": v(33.88, 90) * mm});
            skLineSegment(sketch, "E88", {"start": v(-80, 0) * mm, "end": v(80, 0) * mm, "construction": true});
            skLineSegment(sketch, "E89.MirrorCS", {"start": v(-32.12, -90) * mm, "end": v(-14.12, -108) * mm});
            skLineSegment(sketch, "E90.MirrorCS", {"start": v(-14.12, -108) * mm, "end": v(-14.12, -120) * mm});
            skArc(sketch, "E91.MirrorCS", {"start": v(15.88, -120) * mm, "mid": v(0.88, -135) * mm, "end": v(-14.12, -120) * mm});
            skPoint(sketch, "E92.MirrorP", {"position": v(0.88, -90) * mm});
            skPoint(sketch, "E93.MirrorP", {"position": v(0, -90) * mm});
            skLineSegment(sketch, "E94.MirrorCS", {"start": v(15.88, -108) * mm, "end": v(33.88, -90) * mm});
            skPoint(sketch, "E95.MirrorP", {"position": v(0.88, -135) * mm});
            skLineSegment(sketch, "E96.MirrorCS", {"start": v(15.88, -120) * mm, "end": v(15.88, -108) * mm});
            skCircle(sketch, "E97.MirrorC", {"center": v(0.88, -120) * mm, "radius": 6 * mm});
            skLineSegment(sketch, "E98.MirrorCS", {"start": v(0.88, -90) * mm, "end": v(0.88, -120) * mm, "construction": true});
            skSolve(sketch);
        }
        {
            var Q0;
            {var subQ0=sQuery(id+"F16.wireOp",EDGE,"E89.MirrorCS");Q0=makeQuery(id+"F16.imprint","IMPRINT",FACE,{"disambiguationData":[TD([[makeQuery(id+"F16.imprint","IMPRINT",EDGE,{"derivedFrom":subQ0}),1.0]])]});}
            var Q1;
            {var subQ0=sQuery(id+"F16.wireOp",EDGE,"E79");Q1=makeQuery(id+"F16.imprint","IMPRINT",FACE,{"disambiguationData":[TD([[makeQuery(id+"F16.imprint","IMPRINT",EDGE,{"derivedFrom":subQ0}),-1.0]])]});}
            var Q2;
            Q2=makeQuery(id+"F16.imprint","IMPRINT",FACE,{"disambiguationData":[TD([[makeQuery(id+"F16.imprint","IMPRINT",EDGE,{"derivedFrom":makeQuery(id+"F1.opExtrude","CAP_EDGE",EDGE,{"disambiguationData":[OSD([sQuery(id+"F0.wireOp",EDGE,"E1.left")])],"isStart":true})}),-1.0]])]});
            var Q3;
            Q3=makeQuery(id+"F2.opExtrude","CAP_FACE",FACE,{"disambiguationData":[OSD([sQuery(id+"F0.wireOp",EDGE,"E12"),sQuery(id+"F0.wireOp",EDGE,"E13"),sQuery(id+"F0.wireOp",EDGE,"E14"),sQuery(id+"F0.wireOp",EDGE,"E15"),sQuery(id+"F0.wireOp",EDGE,"E17.filletArc"),sQuery(id+"F0.wireOp",EDGE,"E18.filletArc"),sQuery(id+"F0.wireOp",EDGE,"E19.filletArc"),sQuery(id+"F0.wireOp",EDGE,"E20.filletArc"),sQuery(id+"F0.wireOp",EDGE,"E25.0"),sQuery(id+"F0.wireOp",EDGE,"E25.1"),sQuery(id+"F0.wireOp",EDGE,"E25.2"),sQuery(id+"F0.wireOp",EDGE,"E25.3"),sQuery(id+"F0.wireOp",EDGE,"E25.4"),sQuery(id+"F0.wireOp",EDGE,"E25.5"),sQuery(id+"F0.wireOp",EDGE,"E25.6"),sQuery(id+"F0.wireOp",EDGE,"E25.7")])],"isStart":false});
            extrude(context, id + "F17", {"entities" : qUnion([Q0, Q1, Q2]), "endBound" : BoundingType.UP_TO_SURFACE, "depth" : 25 * mm, "endBoundEntityFace" : qUnion([Q3]), "offsetDistance" : 25 * mm});
        }
    });
